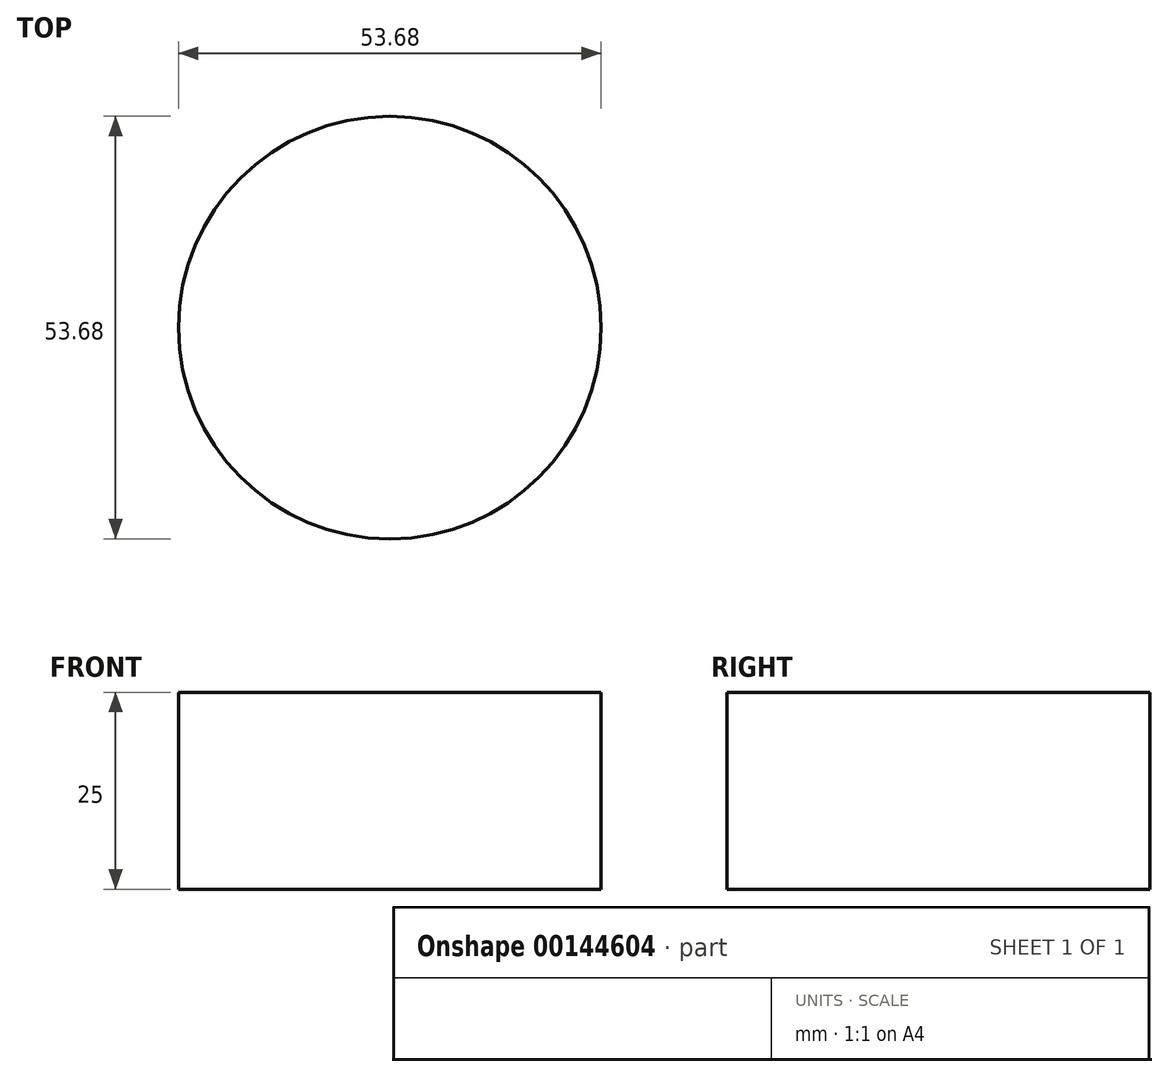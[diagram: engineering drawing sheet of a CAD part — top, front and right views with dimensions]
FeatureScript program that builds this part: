
annotation { "Feature Type Name" : "Feature", "Feature Type Description" : "" }
export const myFeature = defineFeature(function(context is Context, id is Id, definition is map)
    precondition{}
    {
        {
            var Q0;
            Q0=qCreatedBy(makeId("Top.planeOp"),FACE);
            var sketch = newSketch(context, id + "F0", { "sketchPlane" : qUnion([Q0])});
            skCircle(sketch, "E0", {"center": v(0, 0) * mm, "radius": 26.84 * mm});
            skSolve(sketch);
        }
        {
            var Q0;
            Q0=makeQuery(id+"F0.imprint","IMPRINT",FACE,{"disambiguationData":[TD([[makeQuery(id+"F0.imprint","IMPRINT",EDGE,{"derivedFrom":sQuery(id+"F0.wireOp",EDGE,"E0")}),1.0]])]});
            extrude(context, id + "F1", {"entities" : qUnion([Q0]), "depth" : 25 * mm});
        }
    });
